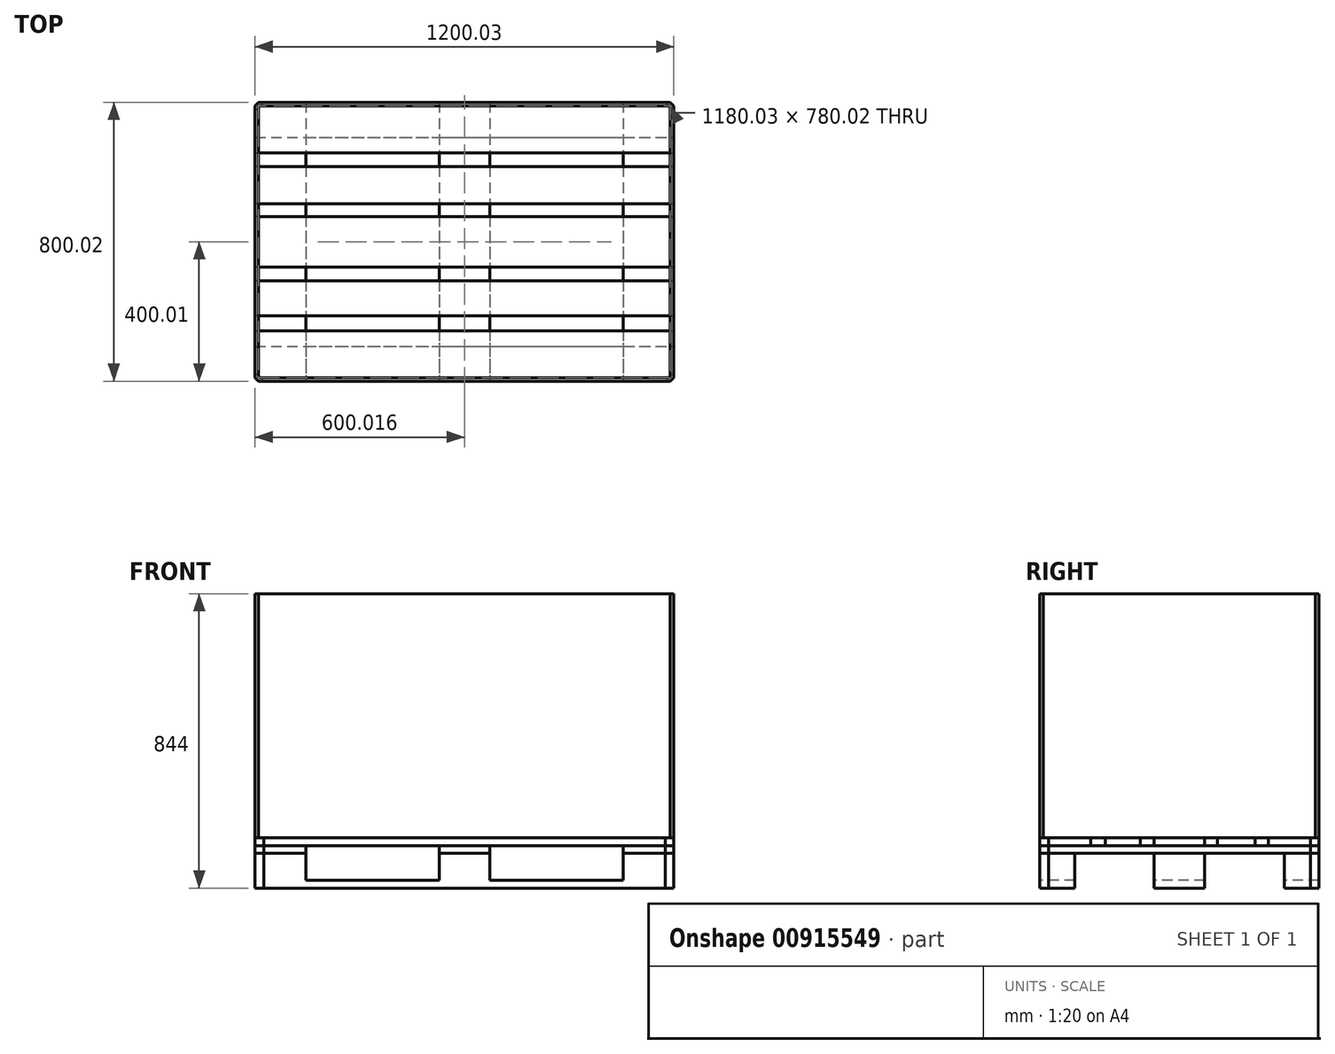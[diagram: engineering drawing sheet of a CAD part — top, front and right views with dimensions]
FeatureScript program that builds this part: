
annotation { "Feature Type Name" : "Feature", "Feature Type Description" : "" }
export const myFeature = defineFeature(function(context is Context, id is Id, definition is map)
    precondition{}
    {
        {
            var Q0;
            Q0=qCreatedBy(makeId("Top.planeOp"),FACE);
            var sketch = newSketch(context, id + "F0", { "sketchPlane" : qUnion([Q0])});
            skLineSegment(sketch, "E0.bottom", {"start": v(600, -400) * mm, "end": v(-600, -400) * mm});
            skLineSegment(sketch, "E0.top", {"start": v(600, 400) * mm, "end": v(-600, 400) * mm});
            skLineSegment(sketch, "E0.left", {"start": v(600, -400) * mm, "end": v(600, 400) * mm});
            skLineSegment(sketch, "E0.right", {"start": v(-600, -400) * mm, "end": v(-600, 400) * mm});
            skPoint(sketch, "E0.middle", {"position": v(0, 0) * mm});
            skLineSegment(sketch, "E1", {"start": v(-600, 300) * mm, "end": v(600, 300) * mm});
            skLineSegment(sketch, "E2", {"start": v(-600, -300) * mm, "end": v(600, -300) * mm});
            skLineSegment(sketch, "E3", {"start": v(-600, 0) * mm, "end": v(600, 0) * mm});
            skLineSegment(sketch, "E4", {"start": v(-600, 72.5) * mm, "end": v(600, 72.5) * mm});
            skLineSegment(sketch, "E5", {"start": v(-600, -72.5) * mm, "end": v(600, -72.5) * mm});
            skSolve(sketch);
        }
        {
            var Q0;
            {var subQ0=sQuery(id+"F0.wireOp",EDGE,"E0.top");Q0=makeQuery(id+"F0.imprint","IMPRINT",FACE,{"disambiguationData":[TD([[makeQuery(id+"F0.imprint","IMPRINT",EDGE,{"derivedFrom":subQ0}),1.0]])]});}
            var Q1;
            {var subQ0=sQuery(id+"F0.wireOp",EDGE,"E3");Q1=makeQuery(id+"F0.imprint","IMPRINT",FACE,{"disambiguationData":[TD([[makeQuery(id+"F0.imprint","IMPRINT",EDGE,{"derivedFrom":subQ0}),1.0]])]});}
            var Q2;
            {var subQ0=sQuery(id+"F0.wireOp",EDGE,"E3");Q2=makeQuery(id+"F0.imprint","IMPRINT",FACE,{"disambiguationData":[TD([[makeQuery(id+"F0.imprint","IMPRINT",EDGE,{"derivedFrom":subQ0}),-1.0]])]});}
            var Q3;
            {var subQ0=sQuery(id+"F0.wireOp",EDGE,"E0.bottom");Q3=makeQuery(id+"F0.imprint","IMPRINT",FACE,{"disambiguationData":[TD([[makeQuery(id+"F0.imprint","IMPRINT",EDGE,{"derivedFrom":subQ0}),-1.0]])]});}
            extrude(context, id + "F1", {"entities" : qUnion([Q0, Q1, Q2, Q3]), "depth" : 22 * mm});
        }
        {
            var Q0;
            Q0=makeQuery(id+"F1.opExtrude","CAP_FACE",FACE,{"disambiguationData":[OSD([sQuery(id+"F0.wireOp",EDGE,"E0.top"),sQuery(id+"F0.wireOp",EDGE,"E0.left"),sQuery(id+"F0.wireOp",EDGE,"E0.right"),sQuery(id+"F0.wireOp",EDGE,"E1")])],"isStart":false});
            var sketch = newSketch(context, id + "F2", { "sketchPlane" : qUnion([Q0])});
            skLineSegment(sketch, "E6", {"start": v(-455, 400) * mm, "end": v(-455, 300) * mm});
            skLineSegment(sketch, "E7", {"start": v(0, 400) * mm, "end": v(0, 300) * mm});
            skLineSegment(sketch, "E8", {"start": v(-72.5, 400) * mm, "end": v(-72.5, 300) * mm});
            skLineSegment(sketch, "E9", {"start": v(72.5, 400) * mm, "end": v(72.5, 300) * mm});
            skLineSegment(sketch, "E10", {"start": v(455, 400) * mm, "end": v(455, 300) * mm});
            skPoint(sketch, "E11.startSnap0", {"position": v(-455, 350) * mm});
            skSolve(sketch);
        }
        {
            var Q0;
            {var subQ0=sQuery(id+"F2.wireOp",EDGE,"E6");Q0=makeQuery(id+"F2.imprint","IMPRINT",FACE,{"disambiguationData":[TD([[makeQuery(id+"F2.imprint","IMPRINT",EDGE,{"derivedFrom":subQ0}),-1.0]])]});}
            var Q1;
            {var subQ0=sQuery(id+"F2.wireOp",EDGE,"E7");Q1=makeQuery(id+"F2.imprint","IMPRINT",FACE,{"disambiguationData":[TD([[makeQuery(id+"F2.imprint","IMPRINT",EDGE,{"derivedFrom":subQ0}),-1.0]])]});}
            var Q2;
            {var subQ0=sQuery(id+"F2.wireOp",EDGE,"E7");Q2=makeQuery(id+"F2.imprint","IMPRINT",FACE,{"disambiguationData":[TD([[makeQuery(id+"F2.imprint","IMPRINT",EDGE,{"derivedFrom":subQ0}),1.0]])]});}
            var Q3;
            {var subQ0=sQuery(id+"F2.wireOp",EDGE,"E10");Q3=makeQuery(id+"F2.imprint","IMPRINT",FACE,{"disambiguationData":[TD([[makeQuery(id+"F2.imprint","IMPRINT",EDGE,{"derivedFrom":subQ0}),1.0]])]});}
            extrude(context, id + "F3", {"entities" : qUnion([Q0, Q1, Q2, Q3]), "operationType" : NewBodyOperationType.ADD, "depth" : 78 * mm});
        }
        {
            var Q0;
            Q0=makeQuery(id+"F1.opExtrude","CAP_FACE",FACE,{"disambiguationData":[OSD([sQuery(id+"F0.wireOp",EDGE,"E0.left"),sQuery(id+"F0.wireOp",EDGE,"E0.right"),sQuery(id+"F0.wireOp",EDGE,"E4"),sQuery(id+"F0.wireOp",EDGE,"E5")])],"isStart":false});
            var sketch = newSketch(context, id + "F4", { "sketchPlane" : qUnion([Q0])});
            skLineSegment(sketch, "E12", {"start": v(-455, 72.5) * mm, "end": v(-455, -72.5) * mm});
            skLineSegment(sketch, "E13", {"start": v(-72.5, 72.5) * mm, "end": v(-72.5, -72.5) * mm});
            skLineSegment(sketch, "E14", {"start": v(72.5, 72.5) * mm, "end": v(72.5, -72.5) * mm});
            skLineSegment(sketch, "E15", {"start": v(455, 72.5) * mm, "end": v(455, -72.5) * mm});
            skSolve(sketch);
        }
        {
            var Q0;
            {var subQ0=sQuery(id+"F4.wireOp",EDGE,"E12");Q0=makeQuery(id+"F4.imprint","IMPRINT",FACE,{"disambiguationData":[TD([[makeQuery(id+"F4.imprint","IMPRINT",EDGE,{"derivedFrom":subQ0}),-1.0]])]});}
            var Q1;
            {var subQ0=sQuery(id+"F4.wireOp",EDGE,"E13");Q1=makeQuery(id+"F4.imprint","IMPRINT",FACE,{"disambiguationData":[TD([[makeQuery(id+"F4.imprint","IMPRINT",EDGE,{"derivedFrom":subQ0}),1.0]])]});}
            var Q2;
            {var subQ0=sQuery(id+"F4.wireOp",EDGE,"E15");Q2=makeQuery(id+"F4.imprint","IMPRINT",FACE,{"disambiguationData":[TD([[makeQuery(id+"F4.imprint","IMPRINT",EDGE,{"derivedFrom":subQ0}),1.0]])]});}
            extrude(context, id + "F5", {"entities" : qUnion([Q0, Q1, Q2]), "operationType" : NewBodyOperationType.ADD, "depth" : 78 * mm});
        }
        {
            var Q0;
            Q0=makeQuery(id+"F1.opExtrude","CAP_FACE",FACE,{"disambiguationData":[OSD([sQuery(id+"F0.wireOp",EDGE,"E0.bottom"),sQuery(id+"F0.wireOp",EDGE,"E0.left"),sQuery(id+"F0.wireOp",EDGE,"E0.right"),sQuery(id+"F0.wireOp",EDGE,"E2")])],"isStart":false});
            var sketch = newSketch(context, id + "F6", { "sketchPlane" : qUnion([Q0])});
            skLineSegment(sketch, "E16", {"start": v(-455, -300) * mm, "end": v(-455, -400) * mm});
            skLineSegment(sketch, "E17", {"start": v(-72.5, -300) * mm, "end": v(-72.5, -400) * mm});
            skLineSegment(sketch, "E18", {"start": v(72.5, -300) * mm, "end": v(72.5, -400) * mm});
            skLineSegment(sketch, "E19", {"start": v(455, -300) * mm, "end": v(455, -400) * mm});
            skSolve(sketch);
        }
        {
            var Q0;
            {var subQ0=sQuery(id+"F6.wireOp",EDGE,"E16");Q0=makeQuery(id+"F6.imprint","IMPRINT",FACE,{"disambiguationData":[TD([[makeQuery(id+"F6.imprint","IMPRINT",EDGE,{"derivedFrom":subQ0}),-1.0]])]});}
            var Q1;
            {var subQ0=sQuery(id+"F6.wireOp",EDGE,"E17");Q1=makeQuery(id+"F6.imprint","IMPRINT",FACE,{"disambiguationData":[TD([[makeQuery(id+"F6.imprint","IMPRINT",EDGE,{"derivedFrom":subQ0}),1.0]])]});}
            var Q2;
            {var subQ0=sQuery(id+"F6.wireOp",EDGE,"E19");Q2=makeQuery(id+"F6.imprint","IMPRINT",FACE,{"disambiguationData":[TD([[makeQuery(id+"F6.imprint","IMPRINT",EDGE,{"derivedFrom":subQ0}),1.0]])]});}
            extrude(context, id + "F7", {"entities" : qUnion([Q0, Q1, Q2]), "operationType" : NewBodyOperationType.ADD, "depth" : 78 * mm});
        }
        {
            var Q0;
            Q0=makeQuery(id+"F3.opExtrude","CAP_FACE",FACE,{"disambiguationData":[OSD([sQuery(id+"F0.wireOp",EDGE,"E0.top"),sQuery(id+"F0.wireOp",EDGE,"E0.right"),sQuery(id+"F0.wireOp",EDGE,"E1"),sQuery(id+"F2.wireOp",EDGE,"E6")])],"isStart":false});
            var sketch = newSketch(context, id + "F8", { "sketchPlane" : qUnion([Q0])});
            skLineSegment(sketch, "E20.bottom", {"start": v(-600, 400) * mm, "end": v(-455, 400) * mm});
            skLineSegment(sketch, "E20.top", {"start": v(-600, -400) * mm, "end": v(-455, -400) * mm});
            skLineSegment(sketch, "E20.left", {"start": v(-600, 400) * mm, "end": v(-600, -400) * mm});
            skLineSegment(sketch, "E20.right", {"start": v(-455, 400) * mm, "end": v(-455, -400) * mm});
            skSolve(sketch);
        }
        {
            var Q0;
            Q0=qSketchRegion(id+"F8",true);
            extrude(context, id + "F9", {"entities" : qUnion([Q0]), "depth" : 22 * mm});
        }
        {
            var Q0;
            Q0=makeQuery(id+"F3.opExtrude","CAP_FACE",FACE,{"disambiguationData":[OSD([sQuery(id+"F0.wireOp",EDGE,"E0.top"),sQuery(id+"F0.wireOp",EDGE,"E1"),sQuery(id+"F2.wireOp",EDGE,"E8"),sQuery(id+"F2.wireOp",EDGE,"E9")])],"isStart":false});
            var sketch = newSketch(context, id + "F10", { "sketchPlane" : qUnion([Q0])});
            skLineSegment(sketch, "E21.bottom", {"start": v(-72.5, 400) * mm, "end": v(72.5, 400) * mm});
            skLineSegment(sketch, "E21.top", {"start": v(-72.5, -400) * mm, "end": v(72.5, -400) * mm});
            skLineSegment(sketch, "E21.left", {"start": v(-72.5, 400) * mm, "end": v(-72.5, -400) * mm});
            skLineSegment(sketch, "E21.right", {"start": v(72.5, 400) * mm, "end": v(72.5, -400) * mm});
            skSolve(sketch);
        }
        {
            var Q0;
            Q0=qSketchRegion(id+"F10",true);
            extrude(context, id + "F11", {"entities" : qUnion([Q0]), "depth" : 22 * mm});
        }
        {
            var Q0;
            Q0=makeQuery(id+"F3.opExtrude","CAP_FACE",FACE,{"disambiguationData":[OSD([sQuery(id+"F0.wireOp",EDGE,"E0.top"),sQuery(id+"F0.wireOp",EDGE,"E0.left"),sQuery(id+"F0.wireOp",EDGE,"E1"),sQuery(id+"F2.wireOp",EDGE,"E10")])],"isStart":false});
            var sketch = newSketch(context, id + "F12", { "sketchPlane" : qUnion([Q0])});
            skLineSegment(sketch, "E22.bottom", {"start": v(455, 400) * mm, "end": v(600, 400) * mm});
            skLineSegment(sketch, "E22.top", {"start": v(455, -400) * mm, "end": v(600, -400) * mm});
            skLineSegment(sketch, "E22.left", {"start": v(455, 400) * mm, "end": v(455, -400) * mm});
            skLineSegment(sketch, "E22.right", {"start": v(600, 400) * mm, "end": v(600, -400) * mm});
            skSolve(sketch);
        }
        {
            var Q0;
            Q0=qSketchRegion(id+"F12",true);
            extrude(context, id + "F13", {"entities" : qUnion([Q0]), "depth" : 22 * mm});
        }
        {
            var Q0;
            Q0=makeQuery(id+"F9.opExtrude","CAP_FACE",FACE,{"disambiguationData":[OSD([sQuery(id+"F8.wireOp",EDGE,"E20.bottom"),sQuery(id+"F8.wireOp",EDGE,"E20.top"),sQuery(id+"F8.wireOp",EDGE,"E20.left"),sQuery(id+"F8.wireOp",EDGE,"E20.right")])],"isStart":false});
            var sketch = newSketch(context, id + "F14", { "sketchPlane" : qUnion([Q0])});
            skLineSegment(sketch, "E23.bottom", {"start": v(-600, 400) * mm, "end": v(600, 400) * mm});
            skLineSegment(sketch, "E23.top", {"start": v(-600, 255) * mm, "end": v(600, 255) * mm});
            skLineSegment(sketch, "E23.left", {"start": v(-600, 400) * mm, "end": v(-600, 255) * mm});
            skLineSegment(sketch, "E23.right", {"start": v(600, 400) * mm, "end": v(600, 255) * mm});
            skSolve(sketch);
        }
        {
            var Q0;
            Q0=qSketchRegion(id+"F14",true);
            extrude(context, id + "F15", {"entities" : qUnion([Q0]), "depth" : 22 * mm});
        }
        {
            var Q0;
            Q0=makeQuery(id+"F11.opExtrude","CAP_FACE",FACE,{"disambiguationData":[OSD([sQuery(id+"F10.wireOp",EDGE,"E21.bottom"),sQuery(id+"F10.wireOp",EDGE,"E21.top"),sQuery(id+"F10.wireOp",EDGE,"E21.left"),sQuery(id+"F10.wireOp",EDGE,"E21.right")])],"isStart":false});
            var sketch = newSketch(context, id + "F16", { "sketchPlane" : qUnion([Q0])});
            skLineSegment(sketch, "E24.bottom", {"start": v(600, 72.5) * mm, "end": v(-600, 72.5) * mm});
            skLineSegment(sketch, "E24.top", {"start": v(600, -72.5) * mm, "end": v(-600, -72.5) * mm});
            skLineSegment(sketch, "E24.left", {"start": v(600, 72.5) * mm, "end": v(600, -72.5) * mm});
            skLineSegment(sketch, "E24.right", {"start": v(-600, 72.5) * mm, "end": v(-600, -72.5) * mm});
            skPoint(sketch, "E24.middle", {"position": v(0, 0) * mm});
            skSolve(sketch);
        }
        {
            var Q0;
            Q0=qSketchRegion(id+"F16",true);
            extrude(context, id + "F17", {"entities" : qUnion([Q0]), "depth" : 22 * mm});
        }
        {
            var Q0;
            Q0=makeQuery(id+"F9.opExtrude","CAP_FACE",FACE,{"disambiguationData":[OSD([sQuery(id+"F8.wireOp",EDGE,"E20.bottom"),sQuery(id+"F8.wireOp",EDGE,"E20.top"),sQuery(id+"F8.wireOp",EDGE,"E20.left"),sQuery(id+"F8.wireOp",EDGE,"E20.right")])],"isStart":false});
            var sketch = newSketch(context, id + "F18", { "sketchPlane" : qUnion([Q0])});
            skLineSegment(sketch, "E25.bottom", {"start": v(-600, -400) * mm, "end": v(600, -400) * mm});
            skLineSegment(sketch, "E25.top", {"start": v(-600, -255) * mm, "end": v(600, -255) * mm});
            skLineSegment(sketch, "E25.left", {"start": v(-600, -400) * mm, "end": v(-600, -255) * mm});
            skLineSegment(sketch, "E25.right", {"start": v(600, -400) * mm, "end": v(600, -255) * mm});
            skSolve(sketch);
        }
        {
            var Q0;
            Q0=qSketchRegion(id+"F18",true);
            extrude(context, id + "F19", {"entities" : qUnion([Q0]), "depth" : 22 * mm});
        }
        {
            var Q0;
            Q0=makeQuery(id+"F9.opExtrude","CAP_FACE",FACE,{"disambiguationData":[OSD([sQuery(id+"F8.wireOp",EDGE,"E20.bottom"),sQuery(id+"F8.wireOp",EDGE,"E20.top"),sQuery(id+"F8.wireOp",EDGE,"E20.left"),sQuery(id+"F8.wireOp",EDGE,"E20.right")])],"isStart":false});
            var sketch = newSketch(context, id + "F20", { "sketchPlane" : qUnion([Q0])});
            skLineSegment(sketch, "E26.bottom", {"start": v(600, 108.92) * mm, "end": v(-600, 108.92) * mm});
            skLineSegment(sketch, "E26.top", {"start": v(600, 216.08) * mm, "end": v(-600, 216.08) * mm});
            skLineSegment(sketch, "E26.left", {"start": v(600, 108.92) * mm, "end": v(600, 216.08) * mm});
            skLineSegment(sketch, "E26.right", {"start": v(-600, 108.92) * mm, "end": v(-600, 216.08) * mm});
            skPoint(sketch, "E26.middle", {"position": v(0, 162.5) * mm});
            skSolve(sketch);
        }
        {
            var Q0;
            Q0=qSketchRegion(id+"F20",true);
            extrude(context, id + "F21", {"entities" : qUnion([Q0]), "depth" : 22 * mm});
        }
        {
            var Q0;
            Q0=makeQuery(id+"F9.opExtrude","CAP_FACE",FACE,{"disambiguationData":[OSD([sQuery(id+"F8.wireOp",EDGE,"E20.bottom"),sQuery(id+"F8.wireOp",EDGE,"E20.top"),sQuery(id+"F8.wireOp",EDGE,"E20.left"),sQuery(id+"F8.wireOp",EDGE,"E20.right")])],"isStart":false});
            var sketch = newSketch(context, id + "F22", { "sketchPlane" : qUnion([Q0])});
            skLineSegment(sketch, "E27.bottom", {"start": v(600, -112.5) * mm, "end": v(-600, -112.5) * mm});
            skLineSegment(sketch, "E27.top", {"start": v(600, -212.5) * mm, "end": v(-600, -212.5) * mm});
            skLineSegment(sketch, "E27.left", {"start": v(600, -112.5) * mm, "end": v(600, -212.5) * mm});
            skLineSegment(sketch, "E27.right", {"start": v(-600, -112.5) * mm, "end": v(-600, -212.5) * mm});
            skPoint(sketch, "E27.middle", {"position": v(0, -162.5) * mm});
            skSolve(sketch);
        }
        {
            var Q0;
            Q0=qSketchRegion(id+"F22",true);
            extrude(context, id + "F23", {"entities" : qUnion([Q0]), "depth" : 22 * mm});
        }
        {
            var Q0;
            Q0=makeQuery(id+"F19.opExtrude","SWEPT_EDGE",EDGE,{"disambiguationData":[OSD([sQuery(id+"F18.wireOp",EDGE,"E25.bottom"),sQuery(id+"F18.wireOp",EDGE,"E25.left")])]});
            var Q1;
            Q1=makeQuery(id+"F9.opExtrude","SWEPT_EDGE",EDGE,{"disambiguationData":[OSD([sQuery(id+"F8.wireOp",EDGE,"E20.top"),sQuery(id+"F8.wireOp",EDGE,"E20.left")])]});
            var Q2;
            {var subQ0=sQuery(id+"F0.wireOp",EDGE,"E0.right");var subQ1=sQuery(id+"F0.wireOp",EDGE,"E0.bottom");Q2=makeQuery(id+"F7.boolean.opBoolean","MERGE",EDGE,{"derivedFrom":[makeQuery(id+"F1.opExtrude","SWEPT_EDGE",EDGE,{"disambiguationData":[OSD([subQ1,subQ0])]}),makeQuery(id+"F7.opExtrude","SWEPT_EDGE",EDGE,{"disambiguationData":[OSD([subQ1,subQ0])]})]});}
            var Q3;
            Q3=makeQuery(id+"F19.opExtrude","SWEPT_EDGE",EDGE,{"disambiguationData":[OSD([sQuery(id+"F18.wireOp",EDGE,"E25.bottom"),sQuery(id+"F18.wireOp",EDGE,"E25.right")])]});
            var Q4;
            Q4=makeQuery(id+"F13.opExtrude","SWEPT_EDGE",EDGE,{"disambiguationData":[OSD([sQuery(id+"F12.wireOp",EDGE,"E22.top"),sQuery(id+"F12.wireOp",EDGE,"E22.right")])]});
            var Q5;
            {var subQ0=sQuery(id+"F0.wireOp",EDGE,"E0.left");var subQ1=sQuery(id+"F0.wireOp",EDGE,"E0.bottom");Q5=makeQuery(id+"F7.boolean.opBoolean","MERGE",EDGE,{"derivedFrom":[makeQuery(id+"F1.opExtrude","SWEPT_EDGE",EDGE,{"disambiguationData":[OSD([subQ1,subQ0])]}),makeQuery(id+"F7.opExtrude","SWEPT_EDGE",EDGE,{"disambiguationData":[OSD([subQ1,subQ0])]})]});}
            var Q6;
            Q6=makeQuery(id+"F15.opExtrude","SWEPT_EDGE",EDGE,{"disambiguationData":[OSD([sQuery(id+"F14.wireOp",EDGE,"E23.bottom"),sQuery(id+"F14.wireOp",EDGE,"E23.right")])]});
            var Q7;
            Q7=makeQuery(id+"F13.opExtrude","SWEPT_EDGE",EDGE,{"disambiguationData":[OSD([sQuery(id+"F12.wireOp",EDGE,"E22.bottom"),sQuery(id+"F12.wireOp",EDGE,"E22.right")])]});
            var Q8;
            {var subQ0=sQuery(id+"F0.wireOp",EDGE,"E0.left");var subQ1=sQuery(id+"F0.wireOp",EDGE,"E0.top");Q8=makeQuery(id+"F3.boolean.opBoolean","MERGE",EDGE,{"derivedFrom":[makeQuery(id+"F1.opExtrude","SWEPT_EDGE",EDGE,{"disambiguationData":[OSD([subQ1,subQ0])]}),makeQuery(id+"F3.opExtrude","SWEPT_EDGE",EDGE,{"disambiguationData":[OSD([subQ1,subQ0])]})]});}
            var Q9;
            Q9=makeQuery(id+"F15.opExtrude","SWEPT_EDGE",EDGE,{"disambiguationData":[OSD([sQuery(id+"F14.wireOp",EDGE,"E23.bottom"),sQuery(id+"F14.wireOp",EDGE,"E23.left")])]});
            var Q10;
            Q10=makeQuery(id+"F9.opExtrude","SWEPT_EDGE",EDGE,{"disambiguationData":[OSD([sQuery(id+"F8.wireOp",EDGE,"E20.bottom"),sQuery(id+"F8.wireOp",EDGE,"E20.left")])]});
            var Q11;
            {var subQ0=sQuery(id+"F0.wireOp",EDGE,"E0.right");var subQ1=sQuery(id+"F0.wireOp",EDGE,"E0.top");Q11=makeQuery(id+"F3.boolean.opBoolean","MERGE",EDGE,{"derivedFrom":[makeQuery(id+"F1.opExtrude","SWEPT_EDGE",EDGE,{"disambiguationData":[OSD([subQ1,subQ0])]}),makeQuery(id+"F3.opExtrude","SWEPT_EDGE",EDGE,{"disambiguationData":[OSD([subQ1,subQ0])]})]});}
            chamfer(context, id + "F24", {"entities" : qUnion([Q0, Q1, Q2, Q3, Q4, Q5, Q6, Q7, Q8, Q9, Q10, Q11]), "width" : 25 * mm, "tangentPropagation" : true});
        }
        {
            var Q0;
            Q0=makeQuery(id+"F15.opExtrude","CAP_FACE",FACE,{"disambiguationData":[OSD([sQuery(id+"F14.wireOp",EDGE,"E23.bottom"),sQuery(id+"F14.wireOp",EDGE,"E23.top"),sQuery(id+"F14.wireOp",EDGE,"E23.left"),sQuery(id+"F14.wireOp",EDGE,"E23.right")])],"isStart":false});
            var sketch = newSketch(context, id + "F25", { "sketchPlane" : qUnion([Q0])});
            skLineSegment(sketch, "E28.bottom", {"start": v(-600, 400) * mm, "end": v(600.03, 400) * mm});
            skLineSegment(sketch, "E28.top", {"start": v(-600, -400.02) * mm, "end": v(600.03, -400.02) * mm});
            skLineSegment(sketch, "E28.left", {"start": v(-600, 400) * mm, "end": v(-600, -400.02) * mm});
            skLineSegment(sketch, "E28.right", {"start": v(600.03, 400) * mm, "end": v(600.03, -400.02) * mm});
            skLineSegment(sketch, "E29.0", {"start": v(-590, 390) * mm, "end": v(590.03, 390) * mm});
            skLineSegment(sketch, "E29.1", {"start": v(-590, 390) * mm, "end": v(-590, -390.02) * mm});
            skLineSegment(sketch, "E29.2", {"start": v(-590, -390.02) * mm, "end": v(590.03, -390.02) * mm});
            skLineSegment(sketch, "E29.3", {"start": v(590.03, 390) * mm, "end": v(590.03, -390.02) * mm});
            skSolve(sketch);
        }
        {
            var Q0;
            {var subQ0=sQuery(id+"F25.wireOp",EDGE,"E28.bottom");var subQ1=sQuery(id+"F14.wireOp",EDGE,"E23.right");var subQ2=sQuery(id+"F14.wireOp",EDGE,"E23.left");var subQ3=sQuery(id+"F14.wireOp",EDGE,"E23.bottom");var subQ4=makeQuery(id+"F15.opExtrude","CAP_FACE",FACE,{"disambiguationData":[OSD([subQ3,sQuery(id+"F14.wireOp",EDGE,"E23.top"),subQ2,subQ1])],"isStart":false});var subQ5=makeQuery(id+"F24.opChamfer","BLEND_EDGE",EDGE,{"blendedFrom":[makeQuery(id+"F15.opExtrude","SWEPT_EDGE",EDGE,{"disambiguationData":[OSD([subQ3,subQ2])]}),subQ4],"blendedInto":[subQ4]});var subQ6=makeQuery(id+"F25.imprint","INTERSECT",VERTEX,{"derivedFrom":[subQ5,subQ0]});Q0=makeQuery(id+"F25.imprint","IMPRINT",FACE,{"disambiguationData":[TD([[makeQuery(id+"F25.imprint","IMPRINT",EDGE,{"disambiguationData":[TD([[subQ6,-1.0]])],"derivedFrom":subQ0}),-1.0]])]});}
            var Q1;
            {var subQ7=sQuery(id+"F25.wireOp",EDGE,"E28.left");var subQ9=sQuery(id+"F25.wireOp",EDGE,"E28.bottom");var subQ10=makeQuery(id+"F25.imprint","INTERSECT",VERTEX,{"derivedFrom":[subQ9,subQ7]});Q1=makeQuery(id+"F25.imprint","IMPRINT",FACE,{"disambiguationData":[TD([[makeQuery(id+"F25.imprint","IMPRINT",EDGE,{"disambiguationData":[TD([[subQ10,-1.0]])],"derivedFrom":subQ9}),-1.0]])]});}
            var Q2;
            {var subQ0=sQuery(id+"F25.wireOp",EDGE,"E28.left");var subQ1=sQuery(id+"F14.wireOp",EDGE,"E23.top");var subQ2=makeQuery(id+"F15.opExtrude","CAP_EDGE",EDGE,{"disambiguationData":[OSD([subQ1])],"isStart":false});var subQ3=makeQuery(id+"F25.imprint","INTERSECT",VERTEX,{"derivedFrom":[subQ2,subQ0]});Q2=makeQuery(id+"F25.imprint","IMPRINT",FACE,{"disambiguationData":[TD([[makeQuery(id+"F25.imprint","IMPRINT",EDGE,{"disambiguationData":[TD([[subQ3,-1.0]])],"derivedFrom":subQ2}),1.0]])]});}
            var Q3;
            {var subQ18=sQuery(id+"F25.wireOp",EDGE,"E28.top");Q3=makeQuery(id+"F25.imprint","IMPRINT",FACE,{"disambiguationData":[TD([[makeQuery(id+"F25.imprint","IMPRINT",EDGE,{"derivedFrom":subQ18}),1.0]])]});}
            var Q4;
            {var subQ1=sQuery(id+"F14.wireOp",EDGE,"E23.right");var subQ8=makeQuery(id+"F15.opExtrude","CAP_EDGE",EDGE,{"disambiguationData":[OSD([subQ1])],"isStart":false});Q4=makeQuery(id+"F25.imprint","IMPRINT",FACE,{"disambiguationData":[TD([[makeQuery(id+"F25.imprint","IMPRINT",EDGE,{"derivedFrom":subQ8}),-1.0]])]});}
            extrude(context, id + "F26", {"entities" : qUnion([Q0, Q1, Q2, Q3, Q4]), "depth" : 700 * mm, "offsetDistance" : 25 * mm});
        }
        {
            var Q0;
            Q0=makeQuery(id+"F26.opExtrude","SWEPT_EDGE",EDGE,{"disambiguationData":[OSD([sQuery(id+"F25.wireOp",EDGE,"E28.top"),sQuery(id+"F25.wireOp",EDGE,"E28.right")])]});
            var Q1;
            Q1=makeQuery(id+"F26.opExtrude","SWEPT_EDGE",EDGE,{"disambiguationData":[OSD([sQuery(id+"F25.wireOp",EDGE,"E28.top"),sQuery(id+"F25.wireOp",EDGE,"E28.left")])]});
            var Q2;
            Q2=makeQuery(id+"F26.opExtrude","SWEPT_EDGE",EDGE,{"disambiguationData":[OSD([sQuery(id+"F25.wireOp",EDGE,"E28.bottom"),sQuery(id+"F25.wireOp",EDGE,"E28.left")])]});
            var Q3;
            Q3=makeQuery(id+"F26.opExtrude","SWEPT_EDGE",EDGE,{"disambiguationData":[OSD([sQuery(id+"F25.wireOp",EDGE,"E28.bottom"),sQuery(id+"F25.wireOp",EDGE,"E28.right")])]});
            chamfer(context, id + "F27", {"entities" : qUnion([Q0, Q1, Q2, Q3]), "width" : 10 * mm, "tangentPropagation" : true});
        }
    });
